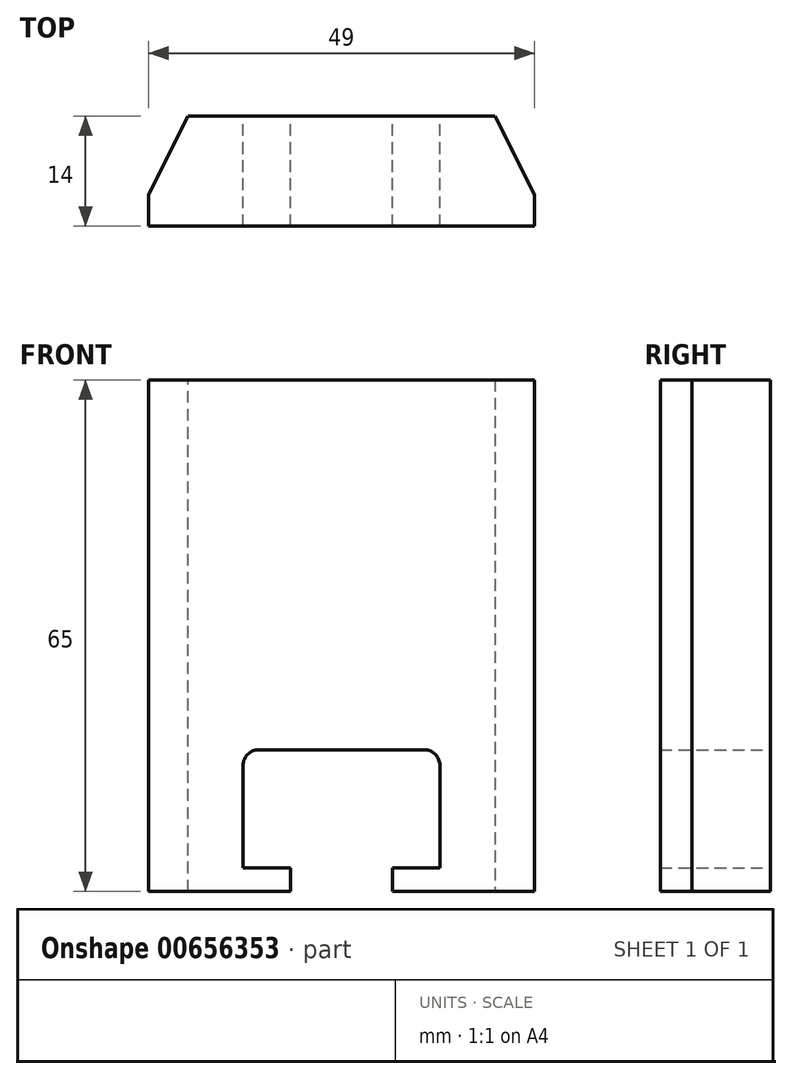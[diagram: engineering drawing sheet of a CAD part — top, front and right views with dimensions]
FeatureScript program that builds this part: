
annotation { "Feature Type Name" : "Feature", "Feature Type Description" : "" }
export const myFeature = defineFeature(function(context is Context, id is Id, definition is map)
    precondition{}
    {
        {
            var Q0;
            Q0=qCreatedBy(makeId("Front.planeOp"),FACE);
            var sketch = newSketch(context, id + "F0", { "sketchPlane" : qUnion([Q0])});
            skLineSegment(sketch, "E0", {"start": v(0, 0) * mm, "end": v(12, 0) * mm});
            skLineSegment(sketch, "E1", {"start": v(12, 0) * mm, "end": v(12, 65) * mm});
            skLineSegment(sketch, "E2", {"start": v(12, 65) * mm, "end": v(-37, 65) * mm});
            skLineSegment(sketch, "E3", {"start": v(-37, 65) * mm, "end": v(-37, 0) * mm});
            skLineSegment(sketch, "E4", {"start": v(-37, 0) * mm, "end": v(-25, 0) * mm});
            skLineSegment(sketch, "E5", {"start": v(-25, 3) * mm, "end": v(-25, 16) * mm});
            skLineSegment(sketch, "E6", {"start": v(-23, 18) * mm, "end": v(-2, 18) * mm});
            skLineSegment(sketch, "E7", {"start": v(0, 16) * mm, "end": v(0, 3) * mm});
            skPoint(sketch, "E8.visualSharp", {"position": v(-25, 18) * mm});
            skArc(sketch, "E8.filletArc", {"start": v(-23, 18) * mm, "mid": v(-24.41, 17.41) * mm, "end": v(-25, 16) * mm});
            skPoint(sketch, "E9.visualSharp", {"position": v(0, 18) * mm});
            skArc(sketch, "E9.filletArc", {"start": v(0, 16) * mm, "mid": v(-0.59, 17.41) * mm, "end": v(-2, 18) * mm});
            skLineSegment(sketch, "E10", {"start": v(-25, 3) * mm, "end": v(-19, 3) * mm});
            skLineSegment(sketch, "E11", {"start": v(-19, 3) * mm, "end": v(-19, 0) * mm});
            skLineSegment(sketch, "E12", {"start": v(-19, 0) * mm, "end": v(-25, 0) * mm});
            skLineSegment(sketch, "E13", {"start": v(0, 3) * mm, "end": v(-6, 3) * mm});
            skLineSegment(sketch, "E14", {"start": v(-6, 3) * mm, "end": v(-6, 0) * mm});
            skLineSegment(sketch, "E15", {"start": v(-6, 0) * mm, "end": v(0, 0) * mm});
            skLineSegment(sketch, "E16", {"start": v(-19, 3) * mm, "end": v(-6, 3) * mm, "construction": true});
            skSolve(sketch);
        }
        {
            var Q0;
            Q0=makeQuery(id+"F0.imprint","IMPRINT",FACE,{"disambiguationData":[TD([[makeQuery(id+"F0.imprint","IMPRINT",EDGE,{"derivedFrom":sQuery(id+"F0.wireOp",EDGE,"E0")}),1.0]])]});
            extrude(context, id + "F1", {"entities" : qUnion([Q0]), "depth" : 14 * mm, "offsetDistance" : 25 * mm});
        }
        {
            var Q0;
            Q0=makeQuery(id+"F1.opExtrude","CAP_EDGE",EDGE,{"disambiguationData":[OSD([sQuery(id+"F0.wireOp",EDGE,"E1")])],"isStart":true});
            var Q1;
            Q1=makeQuery(id+"F1.opExtrude","CAP_EDGE",EDGE,{"disambiguationData":[OSD([sQuery(id+"F0.wireOp",EDGE,"E3")])],"isStart":true});
            chamfer(context, id + "F2", {"entities" : qUnion([Q0, Q1]), "chamferType" : ChamferType.TWO_OFFSETS, "width1" : 10 * mm, "oppositeDirection" : false, "width2" : 5 * mm, "tangentPropagation" : true});
        }
    });
